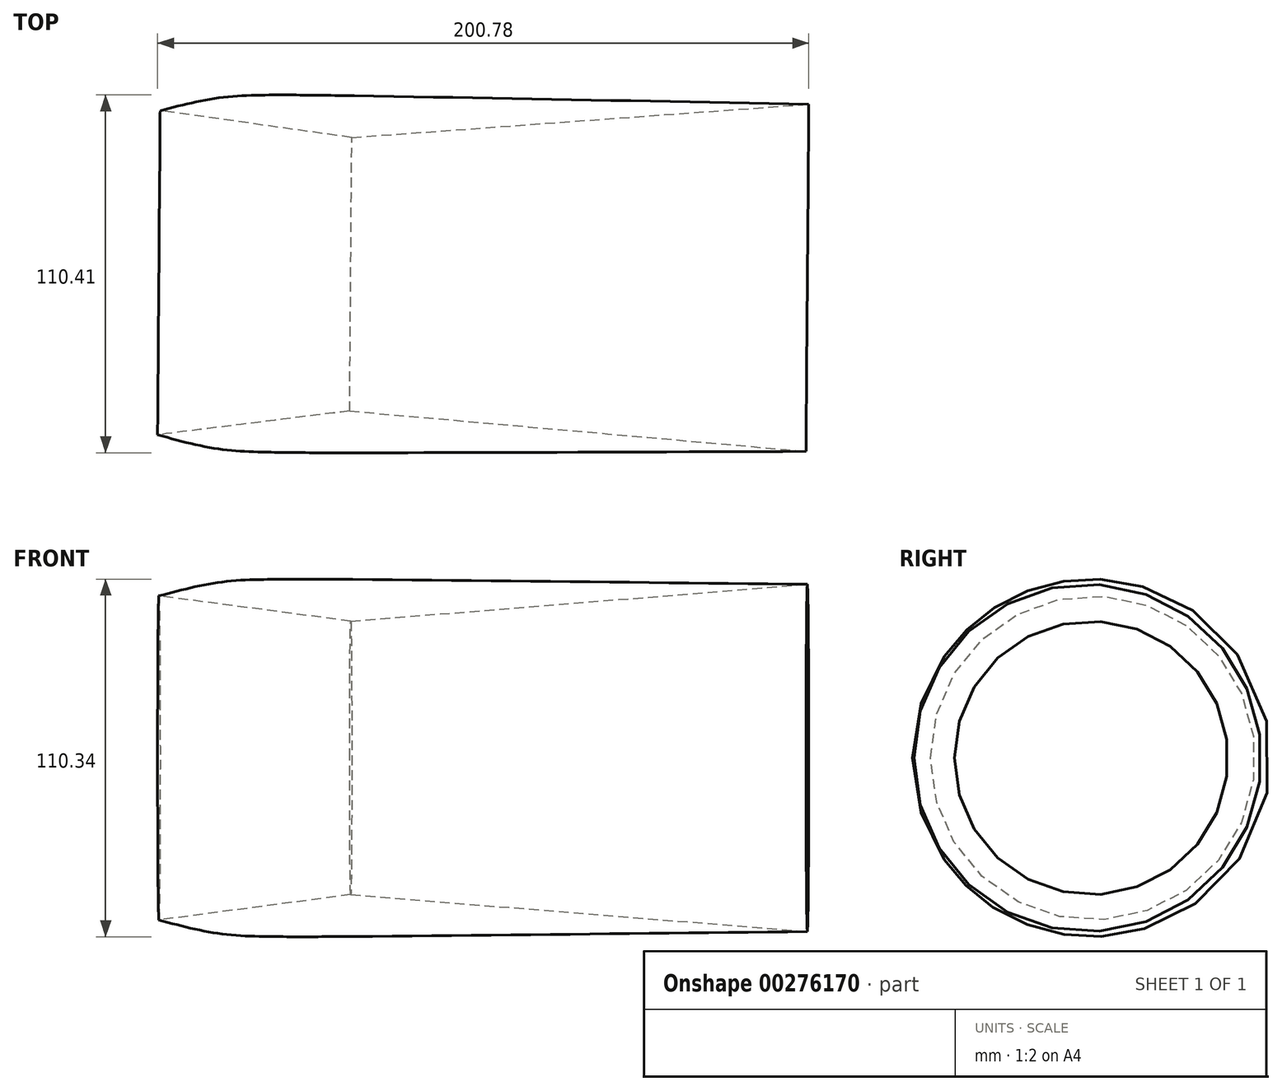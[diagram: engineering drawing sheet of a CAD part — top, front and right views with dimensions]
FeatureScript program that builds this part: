
annotation { "Feature Type Name" : "Feature", "Feature Type Description" : "" }
export const myFeature = defineFeature(function(context is Context, id is Id, definition is map)
    precondition{}
    {
        {
            var Q0;
            Q0=qCreatedBy(makeId("Top.planeOp"),FACE);
            var sketch = newSketch(context, id + "F0", { "sketchPlane" : qUnion([Q0])});
            skFitSpline(sketch, "E0", {"points": [v(-100.6, 36.3) * mm, v(-83.22, 40.19) * mm, v(-68.23, 41.13) * mm, v(-40.79, 40.92) * mm, v(99.4, 38.3) * mm], "startDerivative": vector(106.04, 27.4) * mm, "endDerivative": vector(354.47, -6.89) * mm});
            skLineSegment(sketch, "E1", {"start": v(99.4, 38.3) * mm, "end": v(-41.52, 28.03) * mm});
            skLineSegment(sketch, "E2", {"start": v(-41.52, 28.03) * mm, "end": v(-100.6, 36.3) * mm});
            skLineSegment(sketch, "E3", {"start": v(-68.23, 41.13) * mm, "end": v(-68.23, 31.78) * mm});
            skLineSegment(sketch, "E4", {"start": v(-40.79, 40.92) * mm, "end": v(-41.52, 28.03) * mm});
            skLineSegment(sketch, "E5", {"start": v(-101.65, -13.7) * mm, "end": v(8.89, -14.56) * mm, "construction": true});
            skLineSegment(sketch, "E6", {"start": v(8.89, -14.56) * mm, "end": v(114.63, -14.56) * mm, "construction": true});
            skSolve(sketch);
        }
        {
            var Q0;
            Q0 = qSketchRegion(id + "F0", true);
            var Q1;
            Q1=sQuery(id+"F0.wireOp",EDGE,"E2");
            var Q2;
            Q2=sQuery(id+"F0.wireOp",EDGE,"E1");
            var Q3;
            Q3=sQuery(id+"F0.wireOp",EDGE,"E0");
            var Q4;
            Q4=sQuery(id+"F0.wireOp",EDGE,"E4");
            var Q5;
            Q5=sQuery(id+"F0.wireOp",EDGE,"E3");
            var Q6;
            Q6=sQuery(id+"F0.wireOp",EDGE,"E5");
            revolve(context, id + "F1", {"entities" : qUnion([Q0]), "surfaceEntities" : qUnion([Q1, Q2, Q3, Q4, Q5]), "axis" : qUnion([Q6]), "revolveType" : RevolveType.FULL});
        }
    });
